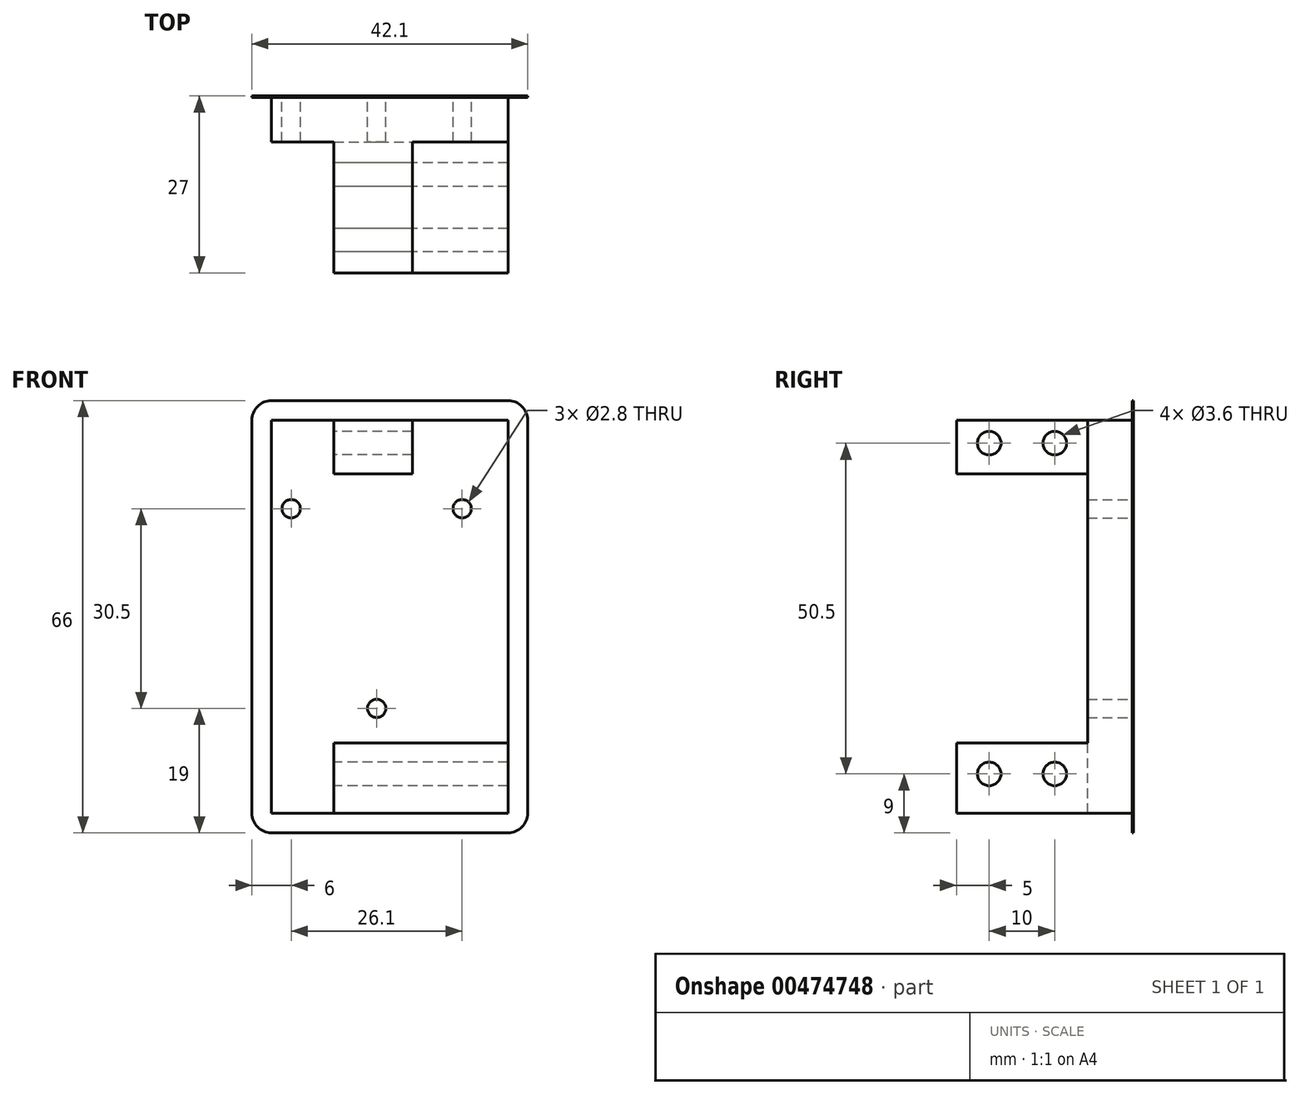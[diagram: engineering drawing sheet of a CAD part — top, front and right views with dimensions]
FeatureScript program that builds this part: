
annotation { "Feature Type Name" : "Feature", "Feature Type Description" : "" }
export const myFeature = defineFeature(function(context is Context, id is Id, definition is map)
    precondition{}
    {
        {
            var Q0;
            Q0=qCreatedBy(makeId("Front.planeOp"),FACE);
            var sketch = newSketch(context, id + "F0", { "sketchPlane" : qUnion([Q0])});
            skLineSegment(sketch, "E0.bottom", {"start": v(0, 40.5) * mm, "end": v(36.1, 40.5) * mm, "construction": true});
            skLineSegment(sketch, "E0.top", {"start": v(0, 0) * mm, "end": v(36.1, 0) * mm, "construction": true});
            skLineSegment(sketch, "E0.left", {"start": v(0, 40.5) * mm, "end": v(0, 0) * mm, "construction": true});
            skLineSegment(sketch, "E0.right", {"start": v(36.1, 40.5) * mm, "end": v(36.1, 0) * mm, "construction": true});
            skLineSegment(sketch, "E1", {"start": v(0, 30.1) * mm, "end": v(42.1, 30.1) * mm, "construction": true});
            skLineSegment(sketch, "E2", {"start": v(42.1, 50.1) * mm, "end": v(40.1, 50.1) * mm, "construction": true});
            skLineSegment(sketch, "E3", {"start": v(42.1, 50.1) * mm, "end": v(42.1, 10.1) * mm, "construction": true});
            skLineSegment(sketch, "E4", {"start": v(42.1, 10.1) * mm, "end": v(40.1, 10.1) * mm, "construction": true});
            skLineSegment(sketch, "E5", {"start": v(40.1, 10.1) * mm, "end": v(40.1, 50.1) * mm, "construction": true});
            skLineSegment(sketch, "E6", {"start": v(26.6, 40.5) * mm, "end": v(26.6, 48) * mm, "construction": true});
            skLineSegment(sketch, "E7", {"start": v(26.6, 48) * mm, "end": v(29.1, 48) * mm, "construction": true});
            skLineSegment(sketch, "E8", {"start": v(29.1, 48) * mm, "end": v(29.1, 40.5) * mm, "construction": true});
            skLineSegment(sketch, "E9", {"start": v(26.6, 0) * mm, "end": v(26.6, -7.5) * mm, "construction": true});
            skLineSegment(sketch, "E10", {"start": v(26.6, -7.5) * mm, "end": v(29.1, -7.5) * mm, "construction": true});
            skLineSegment(sketch, "E11", {"start": v(29.1, -7.5) * mm, "end": v(29.1, 0) * mm, "construction": true});
            skCircle(sketch, "E12", {"center": v(5, 35.5) * mm, "radius": 1.4 * mm});
            skCircle(sketch, "E13", {"center": v(31.1, 35.5) * mm, "radius": 1.4 * mm});
            skLineSegment(sketch, "E14", {"start": v(5, 35.5) * mm, "end": v(31.1, 35.5) * mm, "construction": true});
            skCircle(sketch, "E15", {"center": v(18.05, 5) * mm, "radius": 1.4 * mm});
            skLineSegment(sketch, "E16.top", {"start": v(0, -11) * mm, "end": v(36.1, -11) * mm});
            skLineSegment(sketch, "E17", {"start": v(0, -11) * mm, "end": v(0, 49) * mm});
            skLineSegment(sketch, "E18", {"start": v(0, 49) * mm, "end": v(36.1, 49) * mm});
            skLineSegment(sketch, "E19", {"start": v(36.1, 49) * mm, "end": v(36.1, -11) * mm});
            skLineSegment(sketch, "E20", {"start": v(18.05, 5) * mm, "end": v(18.05, 35.5) * mm, "construction": true});
            skSolve(sketch);
        }
        {
            var Q0;
            Q0=qSketchRegion(id+"F0",true);
            extrude(context, id + "F1", {"entities" : qUnion([Q0]), "depth" : 7 * mm, "offsetDistance" : 25 * mm});
        }
        {
            var Q0;
            Q0=makeQuery(id+"F1.opExtrude","CAP_FACE",FACE,{"disambiguationData":[OSD([sQuery(id+"F0.wireOp",EDGE,"E12"),sQuery(id+"F0.wireOp",EDGE,"E13"),sQuery(id+"F0.wireOp",EDGE,"E15"),sQuery(id+"F0.wireOp",EDGE,"E16.top"),sQuery(id+"F0.wireOp",EDGE,"E17"),sQuery(id+"F0.wireOp",EDGE,"E18"),sQuery(id+"F0.wireOp",EDGE,"E19")])],"isStart":false});
            var sketch = newSketch(context, id + "F2", { "sketchPlane" : qUnion([Q0])});
            skLineSegment(sketch, "E21.bottom", {"start": v(11.5, -11) * mm, "end": v(36.1, -11) * mm});
            skLineSegment(sketch, "E21.top", {"start": v(11.5, -0.3) * mm, "end": v(36.1, -0.3) * mm});
            skLineSegment(sketch, "E21.left", {"start": v(11.5, -11) * mm, "end": v(11.5, -0.3) * mm});
            skLineSegment(sketch, "E21.right", {"start": v(36.1, -11) * mm, "end": v(36.1, -0.3) * mm});
            skLineSegment(sketch, "E22.top", {"start": v(11.5, 40.8) * mm, "end": v(23.5, 40.8) * mm});
            skLineSegment(sketch, "E22.right", {"start": v(23.5, 49) * mm, "end": v(23.5, 40.8) * mm});
            skLineSegment(sketch, "E23", {"start": v(11.5, 40.8) * mm, "end": v(11.5, 49) * mm});
            skLineSegment(sketch, "E24", {"start": v(11.5, 49) * mm, "end": v(23.5, 49) * mm});
            skSolve(sketch);
        }
        {
            var Q0;
            Q0=qSketchRegion(id+"F2",true);
            extrude(context, id + "F3", {"entities" : qUnion([Q0]), "operationType" : NewBodyOperationType.ADD, "depth" : 20 * mm, "offsetDistance" : 25 * mm});
        }
        {
            var Q0;
            Q0=makeQuery(id+"F3.opExtrude","SWEPT_FACE",FACE,{"disambiguationData":[OSD([sQuery(id+"F2.wireOp",EDGE,"E23")])]});
            var sketch = newSketch(context, id + "F4", { "sketchPlane" : qUnion([Q0])});
            skCircle(sketch, "E25", {"center": v(12, 45.5) * mm, "radius": 1.8 * mm});
            skCircle(sketch, "E26", {"center": v(22, 45.5) * mm, "radius": 1.8 * mm});
            skCircle(sketch, "E27", {"center": v(12, -5) * mm, "radius": 1.8 * mm});
            skCircle(sketch, "E28", {"center": v(22, -5) * mm, "radius": 1.8 * mm});
            skLineSegment(sketch, "E29", {"start": v(12, 45.5) * mm, "end": v(22, 45.5) * mm, "construction": true});
            skLineSegment(sketch, "E30", {"start": v(17, 49) * mm, "end": v(17, 40.8) * mm, "construction": true});
            skLineSegment(sketch, "E31", {"start": v(17, -0.3) * mm, "end": v(17, -11) * mm, "construction": true});
            skLineSegment(sketch, "E32", {"start": v(12, -5) * mm, "end": v(22, -5) * mm, "construction": true});
            skSolve(sketch);
        }
        {
            var Q0;
            Q0=qSketchRegion(id+"F4",true);
            var Q1;
            Q1=makeQuery(id+"F3.boolean.opBoolean","MERGE",FACE,{"derivedFrom":[makeQuery(id+"F1.opExtrude","SWEPT_FACE",FACE,{"disambiguationData":[OSD([sQuery(id+"F0.wireOp",EDGE,"E19")])]}),makeQuery(id+"F3.opExtrude","SWEPT_FACE",FACE,{"disambiguationData":[OSD([sQuery(id+"F2.wireOp",EDGE,"E21.right")])]})]});
            extrude(context, id + "F5", {"entities" : qUnion([Q0]), "operationType" : NewBodyOperationType.REMOVE, "endBound" : BoundingType.UP_TO_SURFACE, "oppositeDirection" : true, "depth" : 25 * mm, "endBoundEntityFace" : qUnion([Q1]), "offsetDistance" : 25 * mm});
        }
        {
            var Q0;
            Q0=makeQuery(id+"F3.boolean.opBoolean","MERGE",FACE,{"derivedFrom":[makeQuery(id+"F1.opExtrude","SWEPT_FACE",FACE,{"disambiguationData":[OSD([sQuery(id+"F0.wireOp",EDGE,"E19")])]}),makeQuery(id+"F3.opExtrude","SWEPT_FACE",FACE,{"disambiguationData":[OSD([sQuery(id+"F2.wireOp",EDGE,"E21.right")])]})]});
            var sketch = newSketch(context, id + "F6", { "sketchPlane" : qUnion([Q0])});
            skLineSegment(sketch, "E33", {"start": v(-7, 49) * mm, "end": v(0, 49) * mm});
            skLineSegment(sketch, "E34", {"start": v(0, 49) * mm, "end": v(0, -11) * mm});
            skLineSegment(sketch, "E35", {"start": v(0, -11) * mm, "end": v(-27, -11) * mm});
            skLineSegment(sketch, "E36", {"start": v(-27, -11) * mm, "end": v(-27, -0.3) * mm});
            skLineSegment(sketch, "E37", {"start": v(-27, -0.3) * mm, "end": v(-7, -0.3) * mm});
            skLineSegment(sketch, "E38", {"start": v(-7, -0.3) * mm, "end": v(-7, 49) * mm});
            skCircle(sketch, "E39", {"center": v(-22, -5) * mm, "radius": 1.8 * mm});
            skCircle(sketch, "E40", {"center": v(-12, -5) * mm, "radius": 1.8 * mm});
            skSolve(sketch);
        }
        {
            var Q0;
            Q0 = qSketchRegion(id + "F6", true);
            extrude(context, id + "F7", {"entities" : qUnion([Q0]), "operationType" : NewBodyOperationType.ADD, "depth" : 2 * mm, "offsetDistance" : 25 * mm});
        }
        {
            var Q0;
            Q0=makeQuery(id+"F1.opExtrude","SWEPT_FACE",FACE,{"disambiguationData":[OSD([sQuery(id+"F0.wireOp",EDGE,"E17")])]});
            var sketch = newSketch(context, id + "F8", { "sketchPlane" : qUnion([Q0])});
            skLineSegment(sketch, "E41.bottom", {"start": v(7, 49) * mm, "end": v(0, 49) * mm});
            skLineSegment(sketch, "E41.top", {"start": v(7, -11) * mm, "end": v(0, -11) * mm});
            skLineSegment(sketch, "E41.left", {"start": v(7, 49) * mm, "end": v(7, -11) * mm});
            skLineSegment(sketch, "E41.right", {"start": v(0, 49) * mm, "end": v(0, -11) * mm});
            skSolve(sketch);
        }
        {
            var Q0;
            Q0 = qSketchRegion(id + "F8", true);
            extrude(context, id + "F9", {"entities" : qUnion([Q0]), "operationType" : NewBodyOperationType.REMOVE, "oppositeDirection" : true, "depth" : 2 * mm, "offsetDistance" : 25 * mm});
        }
        {
            var Q0;
            Q0=makeQuery(id+"F0.imprint","IMPRINT",FACE,{"disambiguationData":[TD([[makeQuery(id+"F0.imprint","IMPRINT",EDGE,{"derivedFrom":sQuery(id+"F0.wireOp",EDGE,"E12")}),-1.0]])]});
            var sketch = newSketch(context, id + "F10", { "sketchPlane" : qUnion([Q0])});
            skLineSegment(sketch, "E42", {"start": v(41.1, 49) * mm, "end": v(41.1, -11) * mm});
            skArc(sketch, "E43", {"start": v(38.1, -14) * mm, "mid": v(40.22, -13.12) * mm, "end": v(41.1, -11) * mm});
            skArc(sketch, "E44", {"start": v(41.1, 49) * mm, "mid": v(40.22, 51.12) * mm, "end": v(38.1, 52) * mm});
            skLineSegment(sketch, "E45", {"start": v(38.1, 49) * mm, "end": v(38.1, -11) * mm});
            skLineSegment(sketch, "E46", {"start": v(38.1, 49) * mm, "end": v(2, 49) * mm});
            skLineSegment(sketch, "E47", {"start": v(2, 49) * mm, "end": v(2, -11) * mm});
            skLineSegment(sketch, "E48", {"start": v(38.1, -11) * mm, "end": v(2, -11) * mm});
            skLineSegment(sketch, "E49", {"start": v(38.1, 52) * mm, "end": v(2, 52) * mm});
            skArc(sketch, "E50", {"start": v(2, 52) * mm, "mid": v(-0.12, 51.12) * mm, "end": v(-1, 49) * mm});
            skLineSegment(sketch, "E51", {"start": v(-1, 49) * mm, "end": v(-1, -11) * mm});
            skArc(sketch, "E52", {"start": v(-1, -11) * mm, "mid": v(-0.12, -13.12) * mm, "end": v(2, -14) * mm});
            skLineSegment(sketch, "E53", {"start": v(38.1, -14) * mm, "end": v(2, -14) * mm});
            skSolve(sketch);
        }
        {
            var Q0;
            Q0 = qSketchRegion(id + "F10", true);
            extrude(context, id + "F11", {"entities" : qUnion([Q0]), "operationType" : NewBodyOperationType.ADD, "depth" : 0.2 * mm, "offsetDistance" : 25 * mm});
        }
    });
